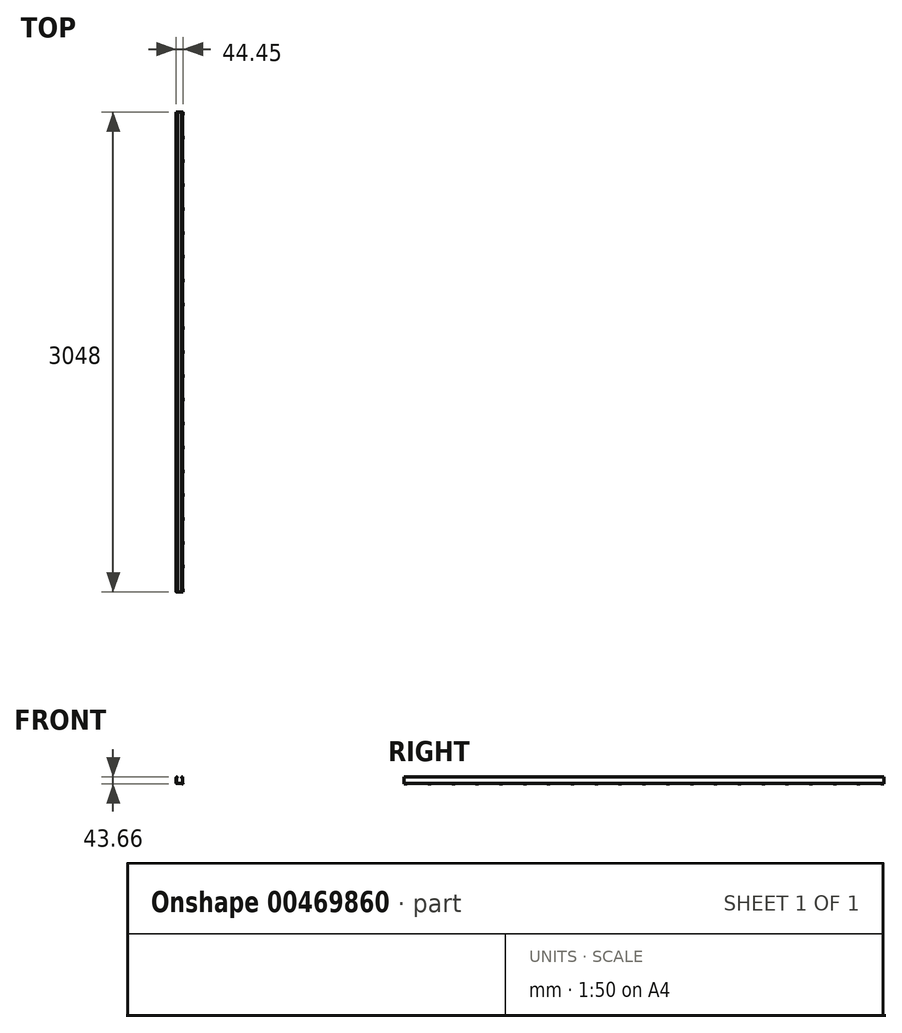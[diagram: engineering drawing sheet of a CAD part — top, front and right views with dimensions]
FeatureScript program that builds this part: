
annotation { "Feature Type Name" : "Feature", "Feature Type Description" : "" }
export const myFeature = defineFeature(function(context is Context, id is Id, definition is map)
    precondition{}
    {
        {
            var Q0;
            Q0=qCreatedBy(makeId("Front.planeOp"),FACE);
            var sketch = newSketch(context, id + "F0", { "sketchPlane" : qUnion([Q0])});
            skLineSegment(sketch, "E0.bottom", {"start": v(20.64, -20.64) * mm, "end": v(-20.64, -20.64) * mm});
            skLineSegment(sketch, "E0.left", {"start": v(20.64, -20.64) * mm, "end": v(20.64, 16.68) * mm});
            skLineSegment(sketch, "E0.right", {"start": v(-20.64, -20.64) * mm, "end": v(-20.64, 16.68) * mm});
            skPoint(sketch, "E0.middle", {"position": v(0, 0) * mm});
            skLineSegment(sketch, "E1.0", {"start": v(-19.05, -19.05) * mm, "end": v(-19.05, 16.68) * mm});
            skLineSegment(sketch, "E2.0", {"start": v(19.05, -19.05) * mm, "end": v(-19.05, -19.05) * mm});
            skLineSegment(sketch, "E3.0", {"start": v(19.05, -19.05) * mm, "end": v(19.05, 16.68) * mm});
            skArc(sketch, "E4", {"start": v(-12.71, 16.68) * mm, "mid": v(-16.68, 20.64) * mm, "end": v(-20.64, 16.68) * mm});
            skArc(sketch, "E5", {"start": v(-14.3, 16.68) * mm, "mid": v(-16.68, 19.05) * mm, "end": v(-19.05, 16.68) * mm});
            skArc(sketch, "E6.MirrorC", {"start": v(12.71, 16.68) * mm, "mid": v(16.68, 20.64) * mm, "end": v(20.64, 16.68) * mm});
            skArc(sketch, "E7.MirrorC", {"start": v(14.3, 16.68) * mm, "mid": v(16.68, 19.05) * mm, "end": v(19.05, 16.68) * mm});
            skPoint(sketch, "E8.orphan", {"position": v(-20.64, 20.64) * mm});
            skLineSegment(sketch, "E9.trimOffspring", {"start": v(-14.3, 16.68) * mm, "end": v(-12.71, 16.68) * mm});
            skLineSegment(sketch, "E10.trimOffspring", {"start": v(12.71, 16.68) * mm, "end": v(14.3, 16.68) * mm});
            skPoint(sketch, "E11.orphan", {"position": v(20.64, 20.64) * mm});
            skSolve(sketch);
        }
        {
            var Q0;
            Q0 = qSketchRegion(id + "F0", true);
            extrude(context, id + "F1", {"entities" : qUnion([Q0]), "endBound" : BoundingType.SYMMETRIC, "depth" : 3048 * mm, "offsetDistance" : 25.4 * mm});
        }
        {
            var Q0;
            Q0=makeQuery(id+"F1.opExtrude","SWEPT_EDGE",EDGE,{"disambiguationData":[OSD([sQuery(id+"F0.wireOp",EDGE,"E0.bottom"),sQuery(id+"F0.wireOp",EDGE,"E0.right")])]});
            var Q1;
            Q1=makeQuery(id+"F1.opExtrude","SWEPT_EDGE",EDGE,{"disambiguationData":[OSD([sQuery(id+"F0.wireOp",EDGE,"E0.bottom"),sQuery(id+"F0.wireOp",EDGE,"E0.left")])]});
            var Q2;
            Q2=makeQuery(id+"F1.opExtrude","SWEPT_EDGE",EDGE,{"disambiguationData":[OSD([sQuery(id+"F0.wireOp",EDGE,"E1.0"),sQuery(id+"F0.wireOp",EDGE,"E2.0")])]});
            var Q3;
            Q3=makeQuery(id+"F1.opExtrude","SWEPT_EDGE",EDGE,{"disambiguationData":[OSD([sQuery(id+"F0.wireOp",EDGE,"E2.0"),sQuery(id+"F0.wireOp",EDGE,"E3.0")])]});
            var Q4;
            Q4=makeQuery(id+"F1.opExtrude","SWEPT_EDGE",EDGE,{"disambiguationData":[OSD([sQuery(id+"F0.wireOp",EDGE,"E7.MirrorC"),sQuery(id+"F0.wireOp",EDGE,"E10.trimOffspring")])]});
            var Q5;
            Q5=makeQuery(id+"F1.opExtrude","SWEPT_EDGE",EDGE,{"disambiguationData":[OSD([sQuery(id+"F0.wireOp",EDGE,"E6.MirrorC"),sQuery(id+"F0.wireOp",EDGE,"E10.trimOffspring")])]});
            var Q6;
            Q6=makeQuery(id+"F1.opExtrude","SWEPT_EDGE",EDGE,{"disambiguationData":[OSD([sQuery(id+"F0.wireOp",EDGE,"E5"),sQuery(id+"F0.wireOp",EDGE,"E9.trimOffspring")])]});
            var Q7;
            Q7=makeQuery(id+"F1.opExtrude","SWEPT_EDGE",EDGE,{"disambiguationData":[OSD([sQuery(id+"F0.wireOp",EDGE,"E4"),sQuery(id+"F0.wireOp",EDGE,"E9.trimOffspring")])]});
            fillet(context, id + "F2", {"entities" : qUnion([Q0, Q1, Q2, Q3, Q4, Q5, Q6, Q7]), "radius" : 0.8 * mm, "tangentPropagation" : true, "allowEdgeOverflow" : false});
        }
        {
            var Q0;
            Q0=makeQuery(id+"F1.opExtrude","SWEPT_FACE",FACE,{"disambiguationData":[OSD([sQuery(id+"F0.wireOp",EDGE,"E0.left")])]});
            var sketch = newSketch(context, id + "F3", { "sketchPlane" : qUnion([Q0])});
            skLineSegment(sketch, "E12.bottom", {"start": v(-1504.95, -23.02) * mm, "end": v(-1524, -23.02) * mm});
            skLineSegment(sketch, "E12.top", {"start": v(-1504.95, -20.5) * mm, "end": v(-1524, -20.5) * mm});
            skLineSegment(sketch, "E12.left", {"start": v(-1504.95, -23.02) * mm, "end": v(-1504.95, -20.5) * mm});
            skLineSegment(sketch, "E12.right", {"start": v(-1524, -23.02) * mm, "end": v(-1524, -20.5) * mm});
            skPoint(sketch, "E12.middle", {"position": v(-1514.48, -21.76) * mm});
            skLineSegment(sketch, "E13.1.0.0", {"start": v(-1353.5, -23.02) * mm, "end": v(-1372.55, -23.02) * mm});
            skLineSegment(sketch, "E13.1.0.1", {"start": v(-1353.5, -20.5) * mm, "end": v(-1372.55, -20.5) * mm});
            skLineSegment(sketch, "E13.1.0.2", {"start": v(-1353.5, -23.02) * mm, "end": v(-1353.5, -20.5) * mm});
            skLineSegment(sketch, "E13.1.0.3", {"start": v(-1372.55, -23.02) * mm, "end": v(-1372.55, -20.5) * mm});
            skLineSegment(sketch, "E13.2.0.0", {"start": v(-1202.06, -23.02) * mm, "end": v(-1221.1, -23.02) * mm});
            skLineSegment(sketch, "E13.2.0.1", {"start": v(-1202.06, -20.5) * mm, "end": v(-1221.1, -20.5) * mm});
            skLineSegment(sketch, "E13.2.0.2", {"start": v(-1202.06, -23.02) * mm, "end": v(-1202.06, -20.5) * mm});
            skLineSegment(sketch, "E13.2.0.3", {"start": v(-1221.1, -23.02) * mm, "end": v(-1221.1, -20.5) * mm});
            skLineSegment(sketch, "E13.3.0.0", {"start": v(-1050.6, -23.02) * mm, "end": v(-1069.66, -23.02) * mm});
            skLineSegment(sketch, "E13.3.0.1", {"start": v(-1050.6, -20.5) * mm, "end": v(-1069.66, -20.5) * mm});
            skLineSegment(sketch, "E13.3.0.2", {"start": v(-1050.6, -23.02) * mm, "end": v(-1050.6, -20.5) * mm});
            skLineSegment(sketch, "E13.3.0.3", {"start": v(-1069.66, -23.02) * mm, "end": v(-1069.66, -20.5) * mm});
            skLineSegment(sketch, "E13.4.0.0", {"start": v(-899.16, -23.02) * mm, "end": v(-918.21, -23.02) * mm});
            skLineSegment(sketch, "E13.4.0.1", {"start": v(-899.16, -20.5) * mm, "end": v(-918.21, -20.5) * mm});
            skLineSegment(sketch, "E13.4.0.2", {"start": v(-899.16, -23.02) * mm, "end": v(-899.16, -20.5) * mm});
            skLineSegment(sketch, "E13.4.0.3", {"start": v(-918.21, -23.02) * mm, "end": v(-918.21, -20.5) * mm});
            skLineSegment(sketch, "E13.5.0.0", {"start": v(-747.71, -23.02) * mm, "end": v(-766.76, -23.02) * mm});
            skLineSegment(sketch, "E13.5.0.1", {"start": v(-747.71, -20.5) * mm, "end": v(-766.76, -20.5) * mm});
            skLineSegment(sketch, "E13.5.0.2", {"start": v(-747.71, -23.02) * mm, "end": v(-747.71, -20.5) * mm});
            skLineSegment(sketch, "E13.5.0.3", {"start": v(-766.76, -23.02) * mm, "end": v(-766.76, -20.5) * mm});
            skLineSegment(sketch, "E13.6.0.0", {"start": v(-596.27, -23.02) * mm, "end": v(-615.32, -23.02) * mm});
            skLineSegment(sketch, "E13.6.0.1", {"start": v(-596.27, -20.5) * mm, "end": v(-615.32, -20.5) * mm});
            skLineSegment(sketch, "E13.6.0.2", {"start": v(-596.27, -23.02) * mm, "end": v(-596.27, -20.5) * mm});
            skLineSegment(sketch, "E13.6.0.3", {"start": v(-615.32, -23.02) * mm, "end": v(-615.32, -20.5) * mm});
            skLineSegment(sketch, "E13.7.0.0", {"start": v(-444.82, -23.02) * mm, "end": v(-463.87, -23.02) * mm});
            skLineSegment(sketch, "E13.7.0.1", {"start": v(-444.82, -20.5) * mm, "end": v(-463.87, -20.5) * mm});
            skLineSegment(sketch, "E13.7.0.2", {"start": v(-444.82, -23.02) * mm, "end": v(-444.82, -20.5) * mm});
            skLineSegment(sketch, "E13.7.0.3", {"start": v(-463.87, -23.02) * mm, "end": v(-463.87, -20.5) * mm});
            skLineSegment(sketch, "E13.8.0.0", {"start": v(-293.37, -23.02) * mm, "end": v(-312.42, -23.02) * mm});
            skLineSegment(sketch, "E13.8.0.1", {"start": v(-293.37, -20.5) * mm, "end": v(-312.42, -20.5) * mm});
            skLineSegment(sketch, "E13.8.0.2", {"start": v(-293.37, -23.02) * mm, "end": v(-293.37, -20.5) * mm});
            skLineSegment(sketch, "E13.8.0.3", {"start": v(-312.42, -23.02) * mm, "end": v(-312.42, -20.5) * mm});
            skLineSegment(sketch, "E13.9.0.0", {"start": v(-141.92, -23.02) * mm, "end": v(-160.97, -23.02) * mm});
            skLineSegment(sketch, "E13.9.0.1", {"start": v(-141.92, -20.5) * mm, "end": v(-160.97, -20.5) * mm});
            skLineSegment(sketch, "E13.9.0.2", {"start": v(-141.92, -23.02) * mm, "end": v(-141.92, -20.5) * mm});
            skLineSegment(sketch, "E13.9.0.3", {"start": v(-160.97, -23.02) * mm, "end": v(-160.97, -20.5) * mm});
            skLineSegment(sketch, "E13.10.0.0", {"start": v(9.52, -23.02) * mm, "end": v(-9.53, -23.02) * mm});
            skLineSegment(sketch, "E13.10.0.1", {"start": v(9.52, -20.5) * mm, "end": v(-9.53, -20.5) * mm});
            skLineSegment(sketch, "E13.10.0.2", {"start": v(9.52, -23.02) * mm, "end": v(9.52, -20.5) * mm});
            skLineSegment(sketch, "E13.10.0.3", {"start": v(-9.53, -23.02) * mm, "end": v(-9.53, -20.5) * mm});
            skLineSegment(sketch, "E13.11.0.0", {"start": v(160.97, -23.02) * mm, "end": v(141.92, -23.02) * mm});
            skLineSegment(sketch, "E13.11.0.1", {"start": v(160.97, -20.5) * mm, "end": v(141.92, -20.5) * mm});
            skLineSegment(sketch, "E13.11.0.2", {"start": v(160.97, -23.02) * mm, "end": v(160.97, -20.5) * mm});
            skLineSegment(sketch, "E13.11.0.3", {"start": v(141.92, -23.02) * mm, "end": v(141.92, -20.5) * mm});
            skLineSegment(sketch, "E13.12.0.0", {"start": v(312.42, -23.02) * mm, "end": v(293.37, -23.02) * mm});
            skLineSegment(sketch, "E13.12.0.1", {"start": v(312.42, -20.5) * mm, "end": v(293.37, -20.5) * mm});
            skLineSegment(sketch, "E13.12.0.2", {"start": v(312.42, -23.02) * mm, "end": v(312.42, -20.5) * mm});
            skLineSegment(sketch, "E13.12.0.3", {"start": v(293.37, -23.02) * mm, "end": v(293.37, -20.5) * mm});
            skLineSegment(sketch, "E13.13.0.0", {"start": v(463.87, -23.02) * mm, "end": v(444.82, -23.02) * mm});
            skLineSegment(sketch, "E13.13.0.1", {"start": v(463.87, -20.5) * mm, "end": v(444.82, -20.5) * mm});
            skLineSegment(sketch, "E13.13.0.2", {"start": v(463.87, -23.02) * mm, "end": v(463.87, -20.5) * mm});
            skLineSegment(sketch, "E13.13.0.3", {"start": v(444.82, -23.02) * mm, "end": v(444.82, -20.5) * mm});
            skLineSegment(sketch, "E13.14.0.0", {"start": v(615.31, -23.02) * mm, "end": v(596.26, -23.02) * mm});
            skLineSegment(sketch, "E13.14.0.1", {"start": v(615.31, -20.5) * mm, "end": v(596.26, -20.5) * mm});
            skLineSegment(sketch, "E13.14.0.2", {"start": v(615.31, -23.02) * mm, "end": v(615.31, -20.5) * mm});
            skLineSegment(sketch, "E13.14.0.3", {"start": v(596.26, -23.02) * mm, "end": v(596.26, -20.5) * mm});
            skLineSegment(sketch, "E13.15.0.0", {"start": v(766.76, -23.02) * mm, "end": v(747.71, -23.02) * mm});
            skLineSegment(sketch, "E13.15.0.1", {"start": v(766.76, -20.5) * mm, "end": v(747.71, -20.5) * mm});
            skLineSegment(sketch, "E13.15.0.2", {"start": v(766.76, -23.02) * mm, "end": v(766.76, -20.5) * mm});
            skLineSegment(sketch, "E13.15.0.3", {"start": v(747.71, -23.02) * mm, "end": v(747.71, -20.5) * mm});
            skLineSegment(sketch, "E13.16.0.0", {"start": v(918.2, -23.02) * mm, "end": v(899.16, -23.02) * mm});
            skLineSegment(sketch, "E13.16.0.1", {"start": v(918.2, -20.5) * mm, "end": v(899.16, -20.5) * mm});
            skLineSegment(sketch, "E13.16.0.2", {"start": v(918.2, -23.02) * mm, "end": v(918.2, -20.5) * mm});
            skLineSegment(sketch, "E13.16.0.3", {"start": v(899.16, -23.02) * mm, "end": v(899.16, -20.5) * mm});
            skLineSegment(sketch, "E13.17.0.0", {"start": v(1069.66, -23.02) * mm, "end": v(1050.6, -23.02) * mm});
            skLineSegment(sketch, "E13.17.0.1", {"start": v(1069.66, -20.5) * mm, "end": v(1050.6, -20.5) * mm});
            skLineSegment(sketch, "E13.17.0.2", {"start": v(1069.66, -23.02) * mm, "end": v(1069.66, -20.5) * mm});
            skLineSegment(sketch, "E13.17.0.3", {"start": v(1050.6, -23.02) * mm, "end": v(1050.6, -20.5) * mm});
            skLineSegment(sketch, "E13.18.0.0", {"start": v(1221.1, -23.02) * mm, "end": v(1202.05, -23.02) * mm});
            skLineSegment(sketch, "E13.18.0.1", {"start": v(1221.1, -20.5) * mm, "end": v(1202.05, -20.5) * mm});
            skLineSegment(sketch, "E13.18.0.2", {"start": v(1221.1, -23.02) * mm, "end": v(1221.1, -20.5) * mm});
            skLineSegment(sketch, "E13.18.0.3", {"start": v(1202.05, -23.02) * mm, "end": v(1202.05, -20.5) * mm});
            skLineSegment(sketch, "E13.19.0.0", {"start": v(1372.55, -23.02) * mm, "end": v(1353.5, -23.02) * mm});
            skLineSegment(sketch, "E13.19.0.1", {"start": v(1372.55, -20.5) * mm, "end": v(1353.5, -20.5) * mm});
            skLineSegment(sketch, "E13.19.0.2", {"start": v(1372.55, -23.02) * mm, "end": v(1372.55, -20.5) * mm});
            skLineSegment(sketch, "E13.19.0.3", {"start": v(1353.5, -23.02) * mm, "end": v(1353.5, -20.5) * mm});
            skLineSegment(sketch, "E13.direction1", {"start": v(-1524, -23.02) * mm, "end": v(-1372.55, -23.02) * mm, "construction": true});
            skLineSegment(sketch, "E14.0.20.0", {"start": v(1524, -23.02) * mm, "end": v(1504.95, -23.02) * mm});
            skLineSegment(sketch, "E14.3.20.0", {"start": v(1524, -20.5) * mm, "end": v(1504.95, -20.5) * mm});
            skLineSegment(sketch, "E14.6.20.0", {"start": v(1524, -23.02) * mm, "end": v(1524, -20.5) * mm});
            skLineSegment(sketch, "E14.9.20.0", {"start": v(1504.95, -23.02) * mm, "end": v(1504.95, -20.5) * mm});
            skSolve(sketch);
        }
        {
            var Q0;
            Q0 = qSketchRegion(id + "F3", true);
            extrude(context, id + "F4", {"entities" : qUnion([Q0]), "operationType" : NewBodyOperationType.ADD, "depth" : 3.17 * mm, "offsetDistance" : 25.4 * mm});
        }
        {
            var Q0;
            Q0=makeQuery(id+"F3.imprint","IMPRINT",FACE,{"disambiguationData":[TD([[makeQuery(id+"F3.imprint","IMPRINT",EDGE,{"derivedFrom":sQuery(id+"F3.wireOp",EDGE,"E12.bottom")}),-1.0]])]});
            var Q1;
            Q1=makeQuery(id+"F3.imprint","IMPRINT",FACE,{"disambiguationData":[TD([[makeQuery(id+"F3.imprint","IMPRINT",EDGE,{"derivedFrom":sQuery(id+"F3.wireOp",EDGE,"E13.1.0.0")}),-1.0]])]});
            var Q2;
            Q2=makeQuery(id+"F3.imprint","IMPRINT",FACE,{"disambiguationData":[TD([[makeQuery(id+"F3.imprint","IMPRINT",EDGE,{"derivedFrom":sQuery(id+"F3.wireOp",EDGE,"E13.2.0.0")}),-1.0]])]});
            var Q3;
            Q3=makeQuery(id+"F3.imprint","IMPRINT",FACE,{"disambiguationData":[TD([[makeQuery(id+"F3.imprint","IMPRINT",EDGE,{"derivedFrom":sQuery(id+"F3.wireOp",EDGE,"E13.3.0.0")}),-1.0]])]});
            var Q4;
            Q4=makeQuery(id+"F3.imprint","IMPRINT",FACE,{"disambiguationData":[TD([[makeQuery(id+"F3.imprint","IMPRINT",EDGE,{"derivedFrom":sQuery(id+"F3.wireOp",EDGE,"E13.4.0.0")}),-1.0]])]});
            var Q5;
            Q5=makeQuery(id+"F3.imprint","IMPRINT",FACE,{"disambiguationData":[TD([[makeQuery(id+"F3.imprint","IMPRINT",EDGE,{"derivedFrom":sQuery(id+"F3.wireOp",EDGE,"E13.5.0.0")}),-1.0]])]});
            var Q6;
            Q6=makeQuery(id+"F3.imprint","IMPRINT",FACE,{"disambiguationData":[TD([[makeQuery(id+"F3.imprint","IMPRINT",EDGE,{"derivedFrom":sQuery(id+"F3.wireOp",EDGE,"E13.6.0.0")}),-1.0]])]});
            var Q7;
            Q7=makeQuery(id+"F3.imprint","IMPRINT",FACE,{"disambiguationData":[TD([[makeQuery(id+"F3.imprint","IMPRINT",EDGE,{"derivedFrom":sQuery(id+"F3.wireOp",EDGE,"E13.7.0.0")}),-1.0]])]});
            var Q8;
            Q8=makeQuery(id+"F3.imprint","IMPRINT",FACE,{"disambiguationData":[TD([[makeQuery(id+"F3.imprint","IMPRINT",EDGE,{"derivedFrom":sQuery(id+"F3.wireOp",EDGE,"E13.8.0.0")}),-1.0]])]});
            var Q9;
            Q9=makeQuery(id+"F3.imprint","IMPRINT",FACE,{"disambiguationData":[TD([[makeQuery(id+"F3.imprint","IMPRINT",EDGE,{"derivedFrom":sQuery(id+"F3.wireOp",EDGE,"E13.9.0.0")}),-1.0]])]});
            var Q10;
            Q10=makeQuery(id+"F3.imprint","IMPRINT",FACE,{"disambiguationData":[TD([[makeQuery(id+"F3.imprint","IMPRINT",EDGE,{"derivedFrom":sQuery(id+"F3.wireOp",EDGE,"E13.10.0.0")}),-1.0]])]});
            var Q11;
            Q11=makeQuery(id+"F3.imprint","IMPRINT",FACE,{"disambiguationData":[TD([[makeQuery(id+"F3.imprint","IMPRINT",EDGE,{"derivedFrom":sQuery(id+"F3.wireOp",EDGE,"E13.11.0.0")}),-1.0]])]});
            var Q12;
            Q12=makeQuery(id+"F3.imprint","IMPRINT",FACE,{"disambiguationData":[TD([[makeQuery(id+"F3.imprint","IMPRINT",EDGE,{"derivedFrom":sQuery(id+"F3.wireOp",EDGE,"E13.12.0.0")}),-1.0]])]});
            var Q13;
            Q13=makeQuery(id+"F3.imprint","IMPRINT",FACE,{"disambiguationData":[TD([[makeQuery(id+"F3.imprint","IMPRINT",EDGE,{"derivedFrom":sQuery(id+"F3.wireOp",EDGE,"E13.13.0.0")}),-1.0]])]});
            var Q14;
            Q14=makeQuery(id+"F3.imprint","IMPRINT",FACE,{"disambiguationData":[TD([[makeQuery(id+"F3.imprint","IMPRINT",EDGE,{"derivedFrom":sQuery(id+"F3.wireOp",EDGE,"E13.14.0.0")}),-1.0]])]});
            var Q15;
            Q15=makeQuery(id+"F3.imprint","IMPRINT",FACE,{"disambiguationData":[TD([[makeQuery(id+"F3.imprint","IMPRINT",EDGE,{"derivedFrom":sQuery(id+"F3.wireOp",EDGE,"E13.15.0.0")}),-1.0]])]});
            var Q16;
            Q16=makeQuery(id+"F3.imprint","IMPRINT",FACE,{"disambiguationData":[TD([[makeQuery(id+"F3.imprint","IMPRINT",EDGE,{"derivedFrom":sQuery(id+"F3.wireOp",EDGE,"E13.17.0.0")}),-1.0]])]});
            var Q17;
            Q17=makeQuery(id+"F3.imprint","IMPRINT",FACE,{"disambiguationData":[TD([[makeQuery(id+"F3.imprint","IMPRINT",EDGE,{"derivedFrom":sQuery(id+"F3.wireOp",EDGE,"E13.16.0.0")}),-1.0]])]});
            var Q18;
            Q18=makeQuery(id+"F3.imprint","IMPRINT",FACE,{"disambiguationData":[TD([[makeQuery(id+"F3.imprint","IMPRINT",EDGE,{"derivedFrom":sQuery(id+"F3.wireOp",EDGE,"E13.18.0.0")}),-1.0]])]});
            var Q19;
            Q19=makeQuery(id+"F3.imprint","IMPRINT",FACE,{"disambiguationData":[TD([[makeQuery(id+"F3.imprint","IMPRINT",EDGE,{"derivedFrom":sQuery(id+"F3.wireOp",EDGE,"E13.19.0.0")}),-1.0]])]});
            var Q20;
            Q20=makeQuery(id+"F3.imprint","IMPRINT",FACE,{"disambiguationData":[TD([[makeQuery(id+"F3.imprint","IMPRINT",EDGE,{"derivedFrom":sQuery(id+"F3.wireOp",EDGE,"E14.0.20.0")}),-1.0]])]});
            extrude(context, id + "F5", {"entities" : qUnion([Q0, Q1, Q2, Q3, Q4, Q5, Q6, Q7, Q8, Q9, Q10, Q11, Q12, Q13, Q14, Q15, Q16, Q17, Q18, Q19, Q20]), "oppositeDirection" : true, "depth" : 2.38 * mm, "offsetDistance" : 25.4 * mm});
        }
    });
